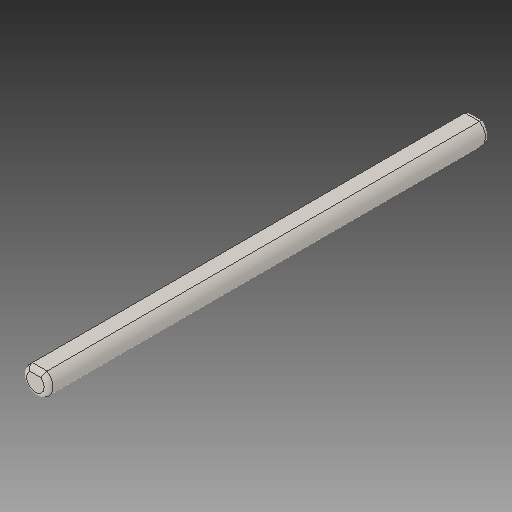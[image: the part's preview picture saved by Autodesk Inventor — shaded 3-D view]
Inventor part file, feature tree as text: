
AUTODESK INVENTOR PART (.ipt)
format: ipt  version: 2018 (Build 220112000, 112)  size: 114,688 bytes
history: native  units: in
note: dims shown in document units (in); Inventor stores cm internally (conversion verified against a paired STEP export)
features: fillet x1
ambient origin geometry x8: Origin, YZ Plane, XZ Plane, XY Plane, X Axis, Y Axis, Z Axis, Center Point
bodies: Solid1 (feature_tree)
feature tree (1):
  fillet  "Fillet1"  [1 undecoded]
note: 1 required parameter value undecoded (feature->parameter linkage not recoverable at this tier; creation-order binding heuristic only, values carry confidence <= 0.55)
